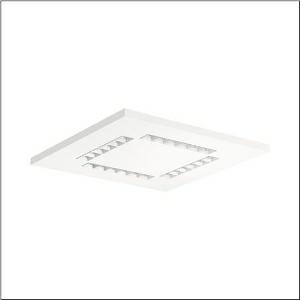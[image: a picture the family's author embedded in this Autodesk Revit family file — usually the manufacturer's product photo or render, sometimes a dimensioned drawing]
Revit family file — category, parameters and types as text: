
# Revit family: silica_r__21_square_51mx6ndu44w_bc45
name_source: partatom
category: Lighting Fixtures
units: mm (PartAtom-declared; Revit-internal decimal feet)

## family parameters
Cut with Voids When Loaded = No
Host = Face
Light Source = No
Part Type = Normal
Room Calculation Point = No
Round Connector Dimension = Use Diameter
Shared = No

## types (1)
- --- (1 x LED, 4600 lm, 27 W, 4000K)
    Apparent Load = 27 VA
    CIE Flux Codes = 83 98 100 100 100
    Color Rendering = 80
    Color Temperature = 4000K
    Default Elevation = 1800 mm
    Description = Silica® 21 Square, office luminaire, primary light control with lens, of PMMA, primary anti-glare with reflector, of PC, white, CAT 2 (L<= 3000cd/m²), light emission: direct distribution, primary light characteristic: symmetric, installation type: lay-in mounting, LED, rated luminous flux: 4.600lm, luminous efficacy: 170lm/W, light colour: 840, colour temperature: 4000K, control gear: DALI 2, with terminal, 5-pole, mains connection: 220..240V, AC, 50/60Hz, rated input power: 27W, luminaire housing, of aluminium, traffic white (RAL 9016), module: M625, length: 622mm, width: 622mm, height: 32mm, protection rating (complete): IP20, insulation class (complete): insulation class I (protective earthing), certification: CE, ENEC, VDE, permissible operating ambient temperature: 0..+35°C, standard: EN 50419, packaging unit: 1 piece
    Height = 0 mm  [stored 0 ft]
    Lamp = 1 x LED
    Lamp Light Flux = 4600 lm
    Lamp Power = 27 W
    Lamp count = 1
    Length = 622 mm
    Luminous efficacy = 170 lm/W
    Manufacturer = Siteco
    ModVariant = No
    Model = 51MX6NDU44W
    Mounting Place = Ceiling
    Mounting Type = Recessed
    Number of Poles = 1
    OnlyDefault = Yes
    Power Factor = 1
    Product Name = Silica® 21 Square
    Product group = office luminaire | ceiling recessed
    ProductGroupID = 400
    Protection Class = Protection class I
    Protection Degree = IP 20
    RLX_Detail_Level = 1
    RLX_Emergency_Light_Flux = 0 lm
    RLX_Emergency_Type = 0
    RLX_Emergency_Type_DB = No
    RlxData = <blob elided: 19029 chars, md5=292ee906>
    Socket = socket
    Standby Power = 0 W
    System Light Flux = 4600 lm
    System Power = 27 W
    Type Comments = factory setting: luminous flux: 100 % | dim-lin: 254 | 366 mA
    Type Image = l_1275224.jpg
    URL = http://relux.com
    VarID = @adj_104879
    Voltage = 0 V
    Weight = 0.00 kg
    Width = 622 mm

note: [stored X ft] marks values corroborated as IEEE doubles in the binary element streams (Revit-internal decimal feet)

## geometry (parser evidence)
native form markers: Blend x4, Sweep x12
no freeform markers — native parametric forms only
